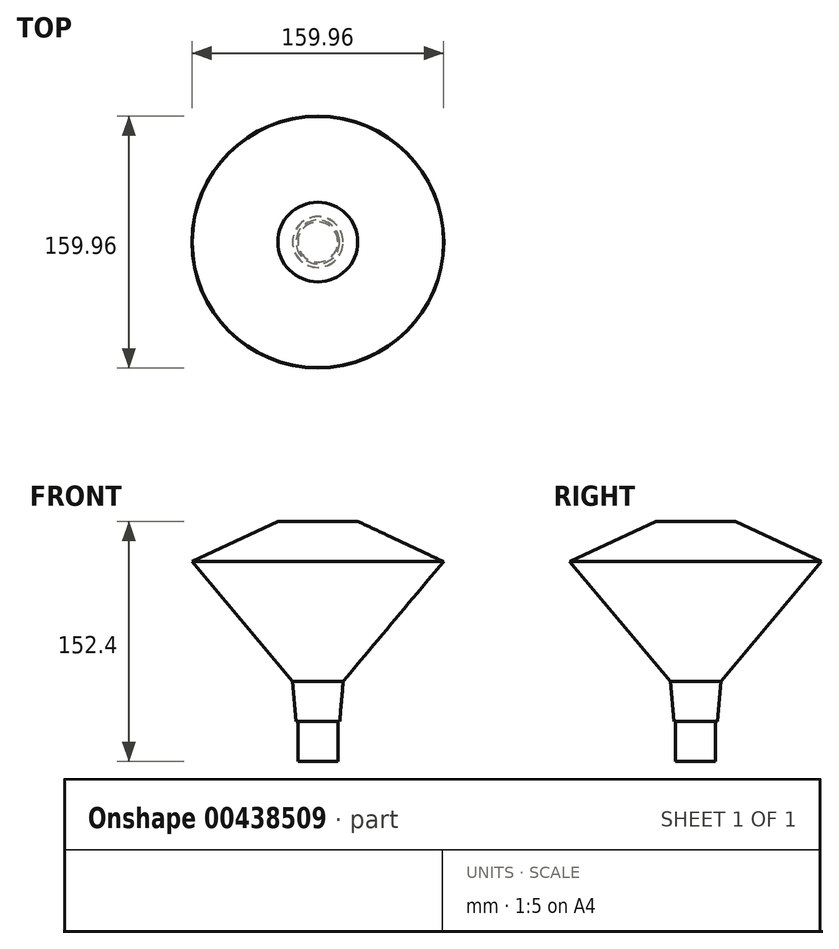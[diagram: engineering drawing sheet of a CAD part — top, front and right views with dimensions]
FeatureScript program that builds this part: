
annotation { "Feature Type Name" : "Feature", "Feature Type Description" : "" }
export const myFeature = defineFeature(function(context is Context, id is Id, definition is map)
    precondition{}
    {
        {
            var Q0;
            Q0=qCreatedBy(makeId("Top.planeOp"),FACE);
            var sketch = newSketch(context, id + "F0", { "sketchPlane" : qUnion([Q0])});
            skCircle(sketch, "E0", {"center": v(0, 0) * mm, "radius": 12.7 * mm});
            skSolve(sketch);
        }
        {
            var Q0;
            Q0 = qSketchRegion(id + "F0", true);
            extrude(context, id + "F1", {"entities" : qUnion([Q0]), "depth" : 25.4 * mm});
        }
        {
            var Q0;
            Q0=makeQuery(id+"F1.opExtrude","CAP_FACE",FACE,{"disambiguationData":[OSD([sQuery(id+"F0.wireOp",EDGE,"E0")])],"isStart":false});
            var sketch = newSketch(context, id + "F2", { "sketchPlane" : qUnion([Q0])});
            skCircle(sketch, "E1", {"center": v(0, 0) * mm, "radius": 13.89 * mm});
            skSolve(sketch);
        }
        {
            var Q0;
            Q0 = qSketchRegion(id + "F2", true);
            extrude(context, id + "F3", {"entities" : qUnion([Q0]), "operationType" : NewBodyOperationType.ADD, "depth" : 25.4 * mm, "hasDraft" : true, "draftAngle" : 5 * degree});
        }
        {
            var Q0;
            Q0=makeQuery(id+"F3.opExtrude","CAP_FACE",FACE,{"disambiguationData":[OSD([sQuery(id+"F2.wireOp",EDGE,"E1")])],"isStart":false});
            var sketch = newSketch(context, id + "F4", { "sketchPlane" : qUnion([Q0])});
            skCircle(sketch, "E2", {"center": v(0, 0) * mm, "radius": 16.04 * mm});
            skSolve(sketch);
        }
        {
            var Q0;
            Q0 = qSketchRegion(id + "F4", true);
            extrude(context, id + "F5", {"entities" : qUnion([Q0]), "operationType" : NewBodyOperationType.ADD, "depth" : 76.2 * mm, "hasDraft" : true, "draftAngle" : 40 * degree});
        }
        {
            var Q0;
            Q0=makeQuery(id+"F5.opExtrude","CAP_FACE",FACE,{"disambiguationData":[OSD([sQuery(id+"F4.wireOp",EDGE,"E2")])],"isStart":false});
            var sketch = newSketch(context, id + "F6", { "sketchPlane" : qUnion([Q0])});
            skCircle(sketch, "E3", {"center": v(0, 0) * mm, "radius": 79.78 * mm});
            skSolve(sketch);
        }
        {
            var Q0;
            Q0 = qSketchRegion(id + "F6", true);
            extrude(context, id + "F7", {"entities" : qUnion([Q0]), "operationType" : NewBodyOperationType.ADD, "depth" : 25.4 * mm, "hasDraft" : true, "draftAngle" : 65 * degree, "draftPullDirection" : true});
        }
    });
